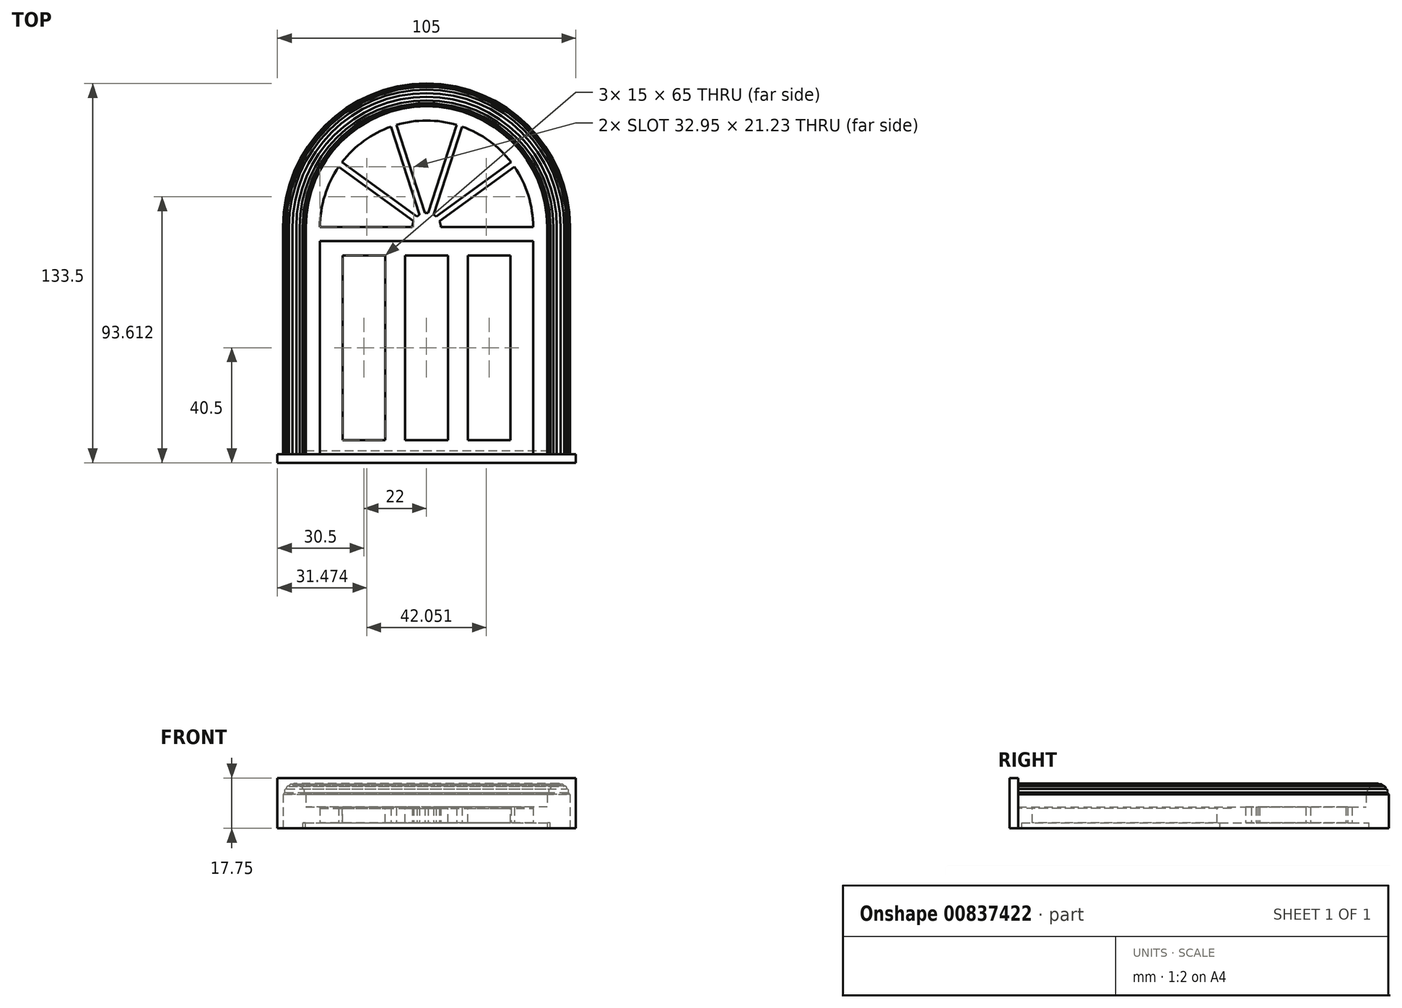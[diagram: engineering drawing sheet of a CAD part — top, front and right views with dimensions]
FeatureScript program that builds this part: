
annotation { "Feature Type Name" : "Feature", "Feature Type Description" : "" }
export const myFeature = defineFeature(function(context is Context, id is Id, definition is map)
    precondition{}
    {
        {
            var Q0;
            Q0=qCreatedBy(makeId("Top.planeOp"),FACE);
            var sketch = newSketch(context, id + "F0", { "sketchPlane" : qUnion([Q0])});
            skLineSegment(sketch, "E0.bottom", {"start": v(-37.5, 75) * mm, "end": v(37.5, 75) * mm});
            skLineSegment(sketch, "E0.top", {"start": v(-37.5, 0) * mm, "end": v(37.5, 0) * mm});
            skLineSegment(sketch, "E0.left", {"start": v(-37.5, 75) * mm, "end": v(-37.5, 0) * mm});
            skLineSegment(sketch, "E0.right", {"start": v(37.5, 75) * mm, "end": v(37.5, 0) * mm});
            skPoint(sketch, "E1", {"position": v(0, 0) * mm});
            skSolve(sketch);
        }
        {
            var Q0;
            Q0=qSketchRegion(id+"F0",true);
            extrude(context, id + "F1", {"entities" : qUnion([Q0]), "depth" : 5 * mm, "offsetDistance" : 25 * mm});
        }
        {
            var Q0;
            Q0=makeQuery(id+"F1.opExtrude","CAP_FACE",FACE,{"disambiguationData":[OSD([sQuery(id+"F0.wireOp",EDGE,"E0.bottom"),sQuery(id+"F0.wireOp",EDGE,"E0.top"),sQuery(id+"F0.wireOp",EDGE,"E0.left"),sQuery(id+"F0.wireOp",EDGE,"E0.right")])],"isStart":false});
            var sketch = newSketch(context, id + "F2", { "sketchPlane" : qUnion([Q0])});
            skLineSegment(sketch, "E2.bottom", {"start": v(-7.5, 70) * mm, "end": v(7.5, 70) * mm});
            skLineSegment(sketch, "E2.top", {"start": v(-7.5, 5) * mm, "end": v(7.5, 5) * mm});
            skLineSegment(sketch, "E2.left", {"start": v(-7.5, 70) * mm, "end": v(-7.5, 5) * mm});
            skLineSegment(sketch, "E2.right", {"start": v(7.5, 70) * mm, "end": v(7.5, 5) * mm});
            skPoint(sketch, "E3", {"position": v(0, 5) * mm});
            skLineSegment(sketch, "E4.bottom", {"start": v(14.5, 70) * mm, "end": v(29.5, 70) * mm});
            skLineSegment(sketch, "E4.top", {"start": v(14.5, 5) * mm, "end": v(29.5, 5) * mm});
            skLineSegment(sketch, "E4.left", {"start": v(14.5, 70) * mm, "end": v(14.5, 5) * mm});
            skLineSegment(sketch, "E4.right", {"start": v(29.5, 70) * mm, "end": v(29.5, 5) * mm});
            skLineSegment(sketch, "E5.bottom", {"start": v(-29.5, 70) * mm, "end": v(-14.5, 70) * mm});
            skLineSegment(sketch, "E5.top", {"start": v(-29.5, 5) * mm, "end": v(-14.5, 5) * mm});
            skLineSegment(sketch, "E5.left", {"start": v(-29.5, 70) * mm, "end": v(-29.5, 5) * mm});
            skLineSegment(sketch, "E5.right", {"start": v(-14.5, 70) * mm, "end": v(-14.5, 5) * mm});
            skSolve(sketch);
        }
        {
            var Q0;
            Q0=qSketchRegion(id+"F2",true);
            extrude(context, id + "F3", {"entities" : qUnion([Q0]), "operationType" : NewBodyOperationType.REMOVE, "oppositeDirection" : true, "depth" : 5 * mm, "offsetDistance" : 25 * mm});
        }
        {
            var Q0;
            Q0=qCreatedBy(makeId("Top.planeOp"),FACE);
            var sketch = newSketch(context, id + "F4", { "sketchPlane" : qUnion([Q0])});
            skLineSegment(sketch, "E6.bottom", {"start": v(-42.5, 0) * mm, "end": v(-37.5, 0) * mm});
            skLineSegment(sketch, "E6.left", {"start": v(-42.5, 0) * mm, "end": v(-42.5, 80) * mm});
            skLineSegment(sketch, "E6.right", {"start": v(-37.5, 0) * mm, "end": v(-37.5, 75) * mm});
            skLineSegment(sketch, "E7", {"start": v(0, 0) * mm, "end": v(0, 80) * mm, "construction": true});
            skLineSegment(sketch, "E8.bottom", {"start": v(-37.5, 80) * mm, "end": v(-5, 80) * mm});
            skLineSegment(sketch, "E8.top", {"start": v(-37.5, 75) * mm, "end": v(0, 75) * mm});
            skLineSegment(sketch, "E8.right", {"start": v(0, 80) * mm, "end": v(0, 75) * mm});
            skArc(sketch, "E9", {"start": v(0, 117.5) * mm, "mid": v(-5.37, 117.11) * mm, "end": v(-10.63, 115.96) * mm});
            skArc(sketch, "E10", {"start": v(0, 122.5) * mm, "mid": v(-30.05, 110.05) * mm, "end": v(-42.5, 80) * mm});
            skLineSegment(sketch, "E11.trimOffspring", {"start": v(0, 117.5) * mm, "end": v(0, 122.5) * mm});
            skArc(sketch, "E12", {"start": v(0, 85) * mm, "mid": v(-0.28, 85) * mm, "end": v(-0.56, 84.97) * mm});
            skLineSegment(sketch, "E13", {"start": v(-34.38, 104.98) * mm, "end": v(0, 80) * mm, "construction": true});
            skLineSegment(sketch, "E14", {"start": v(-13.13, 120.42) * mm, "end": v(0, 80) * mm, "construction": true});
            skLineSegment(sketch, "E15", {"start": v(-30.92, 101.23) * mm, "end": v(-4.55, 82.07) * mm});
            skLineSegment(sketch, "E16", {"start": v(-3.38, 83.69) * mm, "end": v(-29.74, 102.84) * mm});
            skPoint(sketch, "E17", {"position": v(-30.33, 102.03) * mm});
            skPoint(sketch, "E18", {"position": v(-3.96, 82.88) * mm});
            skLineSegment(sketch, "E19", {"start": v(-10.63, 115.96) * mm, "end": v(-0.56, 84.97) * mm});
            skLineSegment(sketch, "E20", {"start": v(-2.46, 84.35) * mm, "end": v(-12.54, 115.34) * mm});
            skPoint(sketch, "E21", {"position": v(-11.58, 115.65) * mm});
            skPoint(sketch, "E22", {"position": v(-1.51, 84.66) * mm});
            skLineSegment(sketch, "E23", {"start": v(0, 80) * mm, "end": v(0, 85) * mm});
            skArc(sketch, "E24.trimOffspring", {"start": v(-30.92, 101.23) * mm, "mid": v(-35.82, 91.11) * mm, "end": v(-37.5, 80) * mm});
            skArc(sketch, "E25.trimOffspring", {"start": v(-12.54, 115.34) * mm, "mid": v(-22.04, 110.34) * mm, "end": v(-29.74, 102.84) * mm});
            skArc(sketch, "E26.trimOffspring", {"start": v(-4.55, 82.07) * mm, "mid": v(-4.89, 81.06) * mm, "end": v(-5, 80) * mm});
            skArc(sketch, "E27.trimOffspring", {"start": v(-2.46, 84.35) * mm, "mid": v(-2.94, 84.05) * mm, "end": v(-3.38, 83.69) * mm});
            skArc(sketch, "E28.MirrorCS", {"start": v(4.55, 82.07) * mm, "mid": v(4.89, 81.06) * mm, "end": v(5, 80) * mm});
            skArc(sketch, "E29.MirrorCS", {"start": v(0, 85) * mm, "mid": v(0.28, 85) * mm, "end": v(0.56, 84.97) * mm});
            skArc(sketch, "E30.MirrorCS", {"start": v(2.46, 84.35) * mm, "mid": v(2.94, 84.05) * mm, "end": v(3.38, 83.69) * mm});
            skLineSegment(sketch, "E31.MirrorCS", {"start": v(42.5, 0) * mm, "end": v(37.5, 0) * mm});
            skLineSegment(sketch, "E32.MirrorCS", {"start": v(37.5, 80) * mm, "end": v(5, 80) * mm});
            skLineSegment(sketch, "E33.MirrorCS", {"start": v(37.5, 75) * mm, "end": v(0, 75) * mm});
            skPoint(sketch, "E34.MirrorP", {"position": v(1.51, 84.66) * mm});
            skArc(sketch, "E35.MirrorCS", {"start": v(30.92, 101.23) * mm, "mid": v(35.82, 91.11) * mm, "end": v(37.5, 80) * mm});
            skLineSegment(sketch, "E36.MirrorCS", {"start": v(2.46, 84.35) * mm, "end": v(12.54, 115.34) * mm});
            skPoint(sketch, "E37.MirrorP", {"position": v(11.58, 115.65) * mm});
            skArc(sketch, "E38.MirrorCS", {"start": v(0, 117.5) * mm, "mid": v(5.37, 117.11) * mm, "end": v(10.63, 115.96) * mm});
            skLineSegment(sketch, "E39.MirrorCS", {"start": v(3.38, 83.69) * mm, "end": v(29.74, 102.84) * mm});
            skLineSegment(sketch, "E40.MirrorCS", {"start": v(13.13, 120.42) * mm, "end": v(0, 80) * mm, "construction": true});
            skArc(sketch, "E41.MirrorCS", {"start": v(0, 122.5) * mm, "mid": v(30.05, 110.05) * mm, "end": v(42.5, 80) * mm});
            skLineSegment(sketch, "E42.MirrorCS", {"start": v(10.63, 115.96) * mm, "end": v(0.56, 84.97) * mm});
            skPoint(sketch, "E43.MirrorP", {"position": v(30.33, 102.03) * mm});
            skLineSegment(sketch, "E44.MirrorCS", {"start": v(42.5, 0) * mm, "end": v(42.5, 80) * mm});
            skLineSegment(sketch, "E45.MirrorCS", {"start": v(34.38, 104.98) * mm, "end": v(0, 80) * mm, "construction": true});
            skArc(sketch, "E46.MirrorCS", {"start": v(12.54, 115.34) * mm, "mid": v(22.04, 110.34) * mm, "end": v(29.74, 102.84) * mm});
            skLineSegment(sketch, "E47.MirrorCS", {"start": v(30.92, 101.23) * mm, "end": v(4.55, 82.07) * mm});
            skLineSegment(sketch, "E48.MirrorCS", {"start": v(37.5, 0) * mm, "end": v(37.5, 75) * mm});
            skPoint(sketch, "E49.MirrorP", {"position": v(3.96, 82.88) * mm});
            skSolve(sketch);
        }
        {
            var Q0;
            Q0=qSketchRegion(id+"F4",true);
            extrude(context, id + "F5", {"entities" : qUnion([Q0]), "operationType" : NewBodyOperationType.ADD, "depth" : 5.5 * mm, "offsetDistance" : 25 * mm});
        }
        {
            var Q0;
            Q0=qCreatedBy(makeId("Top.planeOp"),FACE);
            var sketch = newSketch(context, id + "F6", { "sketchPlane" : qUnion([Q0])});
            skLineSegment(sketch, "E50.bottom", {"start": v(-42.5, 0) * mm, "end": v(-50.5, 0) * mm});
            skLineSegment(sketch, "E50.left", {"start": v(-42.5, 0) * mm, "end": v(-42.5, 80) * mm});
            skLineSegment(sketch, "E50.right", {"start": v(-50.5, 0) * mm, "end": v(-50.5, 80) * mm});
            skArc(sketch, "E51", {"start": v(0, 122.5) * mm, "mid": v(-30.05, 110.05) * mm, "end": v(-42.5, 80) * mm});
            skArc(sketch, "E52", {"start": v(0, 130.5) * mm, "mid": v(-35.7, 115.7) * mm, "end": v(-50.5, 80) * mm});
            skLineSegment(sketch, "E53", {"start": v(0, 122.5) * mm, "end": v(0, 130.5) * mm});
            skLineSegment(sketch, "E54.MirrorCS", {"start": v(42.5, 0) * mm, "end": v(50.5, 0) * mm});
            skLineSegment(sketch, "E55.MirrorCS", {"start": v(42.5, 0) * mm, "end": v(42.5, 80) * mm});
            skLineSegment(sketch, "E56.MirrorCS", {"start": v(50.5, 0) * mm, "end": v(50.5, 80) * mm});
            skArc(sketch, "E57.MirrorCS", {"start": v(0, 122.5) * mm, "mid": v(30.05, 110.05) * mm, "end": v(42.5, 80) * mm});
            skArc(sketch, "E58.MirrorCS", {"start": v(0, 130.5) * mm, "mid": v(35.7, 115.7) * mm, "end": v(50.5, 80) * mm});
            skSolve(sketch);
        }
        {
            var Q0;
            Q0=qSketchRegion(id+"F6",true);
            extrude(context, id + "F7", {"entities" : qUnion([Q0]), "operationType" : NewBodyOperationType.ADD, "depth" : 10 * mm, "offsetDistance" : 25 * mm});
        }
        {
            var Q0;
            Q0=makeQuery(id+"F5.opExtrude","SWEPT_FACE",FACE,{"disambiguationData":[OSD([sQuery(id+"F4.wireOp",EDGE,"E32.MirrorCS")])]});
            var sketch = newSketch(context, id + "F8", { "sketchPlane" : qUnion([Q0])});
            skLineSegment(sketch, "E59", {"start": v(46.5, 10) * mm, "end": v(44, 10) * mm});
            skCircle(sketch, "E60", {"center": v(46.5, 10) * mm, "radius": 3 * mm, "construction": true});
            skArc(sketch, "E61", {"start": v(50.25, 10) * mm, "mid": v(50.14, 10.39) * mm, "end": v(49.85, 10.67) * mm});
            skArc(sketch, "E62.1.0", {"start": v(49.85, 10.67) * mm, "mid": v(49.96, 11.44) * mm, "end": v(49.34, 11.9) * mm});
            skArc(sketch, "E62.2.0", {"start": v(49.34, 11.9) * mm, "mid": v(49.15, 12.65) * mm, "end": v(48.4, 12.84) * mm});
            skArc(sketch, "E62.3.0", {"start": v(48.4, 12.84) * mm, "mid": v(47.94, 13.46) * mm, "end": v(47.17, 13.35) * mm});
            skArc(sketch, "E62.4.0", {"start": v(47.17, 13.35) * mm, "mid": v(46.5, 13.75) * mm, "end": v(45.83, 13.35) * mm});
            skArc(sketch, "E62.5.0", {"start": v(45.83, 13.35) * mm, "mid": v(45.06, 13.46) * mm, "end": v(44.6, 12.84) * mm});
            skArc(sketch, "E62.6.0", {"start": v(44.6, 12.84) * mm, "mid": v(43.85, 12.65) * mm, "end": v(43.66, 11.9) * mm});
            skArc(sketch, "E62.7.0", {"start": v(43.66, 11.9) * mm, "mid": v(43.04, 11.44) * mm, "end": v(43.15, 10.67) * mm});
            skArc(sketch, "E62.8.0", {"start": v(43.15, 10.67) * mm, "mid": v(42.86, 10.39) * mm, "end": v(42.75, 10) * mm});
            skLineSegment(sketch, "E62.anchor2", {"start": v(46.5, 10) * mm, "end": v(44.25, 10) * mm, "construction": true});
            skLineSegment(sketch, "E63", {"start": v(46.5, 10) * mm, "end": v(50.25, 10) * mm});
            skLineSegment(sketch, "E64", {"start": v(50.25, 10) * mm, "end": v(42.75, 10) * mm});
            skLineSegment(sketch, "E65.MirrorCS", {"start": v(-46.5, 10) * mm, "end": v(-44, 10) * mm});
            skArc(sketch, "E66.MirrorCS", {"start": v(-49.85, 10.67) * mm, "mid": v(-49.96, 11.44) * mm, "end": v(-49.34, 11.9) * mm});
            skArc(sketch, "E67.MirrorCS", {"start": v(-45.83, 13.35) * mm, "mid": v(-45.06, 13.46) * mm, "end": v(-44.6, 12.84) * mm});
            skArc(sketch, "E68.MirrorCS", {"start": v(-50.25, 10) * mm, "mid": v(-50.14, 10.39) * mm, "end": v(-49.85, 10.67) * mm});
            skArc(sketch, "E69.MirrorCS", {"start": v(-44.6, 12.84) * mm, "mid": v(-43.85, 12.65) * mm, "end": v(-43.66, 11.9) * mm});
            skArc(sketch, "E70.MirrorCS", {"start": v(-47.17, 13.35) * mm, "mid": v(-46.5, 13.75) * mm, "end": v(-45.83, 13.35) * mm});
            skLineSegment(sketch, "E71.MirrorCS", {"start": v(-46.5, 10) * mm, "end": v(-44.25, 10) * mm, "construction": true});
            skArc(sketch, "E72.MirrorCS", {"start": v(-43.15, 10.67) * mm, "mid": v(-42.86, 10.39) * mm, "end": v(-42.75, 10) * mm});
            skArc(sketch, "E73.MirrorCS", {"start": v(-49.34, 11.9) * mm, "mid": v(-49.15, 12.65) * mm, "end": v(-48.4, 12.84) * mm});
            skArc(sketch, "E74.MirrorCS", {"start": v(-43.66, 11.9) * mm, "mid": v(-43.04, 11.44) * mm, "end": v(-43.15, 10.67) * mm});
            skArc(sketch, "E75.MirrorCS", {"start": v(-48.4, 12.84) * mm, "mid": v(-47.94, 13.46) * mm, "end": v(-47.17, 13.35) * mm});
            skLineSegment(sketch, "E76.MirrorCS", {"start": v(-46.5, 10) * mm, "end": v(-50.25, 10) * mm});
            skLineSegment(sketch, "E77.MirrorCS", {"start": v(-50.25, 10) * mm, "end": v(-42.75, 10) * mm});
            skCircle(sketch, "E78.MirrorC", {"center": v(-46.5, 10) * mm, "radius": 3 * mm, "construction": true});
            skSolve(sketch);
        }
        {
            var Q0;
            Q0=qSketchRegion(id+"F8",true);
            var Q1;
            Q1=makeQuery(id+"F7.opExtrude","CAP_EDGE",EDGE,{"disambiguationData":[OSD([sQuery(id+"F6.wireOp",EDGE,"E51"),sQuery(id+"F6.wireOp",EDGE,"E57.MirrorCS")])],"isStart":false});
            sweep(context, id + "F9", {"operationType" : NewBodyOperationType.ADD, "profiles" : qUnion([Q0]), "path" : qUnion([Q1])});
        }
        {
            var Q0;
            Q0=makeQuery(id+"F7.opExtrude","CAP_FACE",FACE,{"disambiguationData":[OSD([sQuery(id+"F6.wireOp",EDGE,"E50.bottom"),sQuery(id+"F6.wireOp",EDGE,"E50.left"),sQuery(id+"F6.wireOp",EDGE,"E50.right"),sQuery(id+"F6.wireOp",EDGE,"E51"),sQuery(id+"F6.wireOp",EDGE,"E52"),sQuery(id+"F6.wireOp",EDGE,"E54.MirrorCS"),sQuery(id+"F6.wireOp",EDGE,"E55.MirrorCS"),sQuery(id+"F6.wireOp",EDGE,"E56.MirrorCS"),sQuery(id+"F6.wireOp",EDGE,"E57.MirrorCS"),sQuery(id+"F6.wireOp",EDGE,"E58.MirrorCS")])],"isStart":false});
            var sketch = newSketch(context, id + "F10", { "sketchPlane" : qUnion([Q0])});
            skLineSegment(sketch, "E79", {"start": v(0, 80) * mm, "end": v(0, 130.5) * mm, "construction": true});
            skLineSegment(sketch, "E80", {"start": v(0, 80) * mm, "end": v(6.15, 130.12) * mm, "construction": true});
            skLineSegment(sketch, "E81", {"start": v(0, 80) * mm, "end": v(-6.15, 130.12) * mm, "construction": true});
            skLineSegment(sketch, "E82", {"start": v(-6.15, 130.12) * mm, "end": v(-5.18, 122.18) * mm});
            skLineSegment(sketch, "E83", {"start": v(6.15, 130.12) * mm, "end": v(5.18, 122.18) * mm});
            skArc(sketch, "E84", {"start": v(6.15, 130.12) * mm, "mid": v(0, 130.5) * mm, "end": v(-6.15, 130.12) * mm});
            skArc(sketch, "E85", {"start": v(5.18, 122.18) * mm, "mid": v(0, 122.5) * mm, "end": v(-5.18, 122.18) * mm});
            skSolve(sketch);
        }
        {
            var Q0;
            Q0 = qSketchRegion(id + "F8", true);
            var Q1;
            Q1=makeQuery(id+"F7.opExtrude","CAP_EDGE",EDGE,{"disambiguationData":[OSD([sQuery(id+"F6.wireOp",EDGE,"E50.left")])],"isStart":false});
            sweep(context, id + "F11", {"operationType" : NewBodyOperationType.ADD, "profiles" : qUnion([Q0]), "path" : qUnion([Q1])});
        }
        {
            var Q0;
            {var subQ0=sQuery(id+"F6.wireOp",EDGE,"E50.left");var subQ1=sQuery(id+"F6.wireOp",EDGE,"E50.bottom");Q0=makeQuery(id+"F11.boolean.opBoolean","MERGE",FACE,{"derivedFrom":[makeQuery(id+"F7.boolean.opBoolean","MERGE",FACE,{"derivedFrom":[makeQuery(id+"F5.boolean.opBoolean","MERGE",FACE,{"derivedFrom":[makeQuery(id+"F1.opExtrude","SWEPT_FACE",FACE,{"disambiguationData":[OSD([sQuery(id+"F0.wireOp",EDGE,"E0.top")])]}),makeQuery(id+"F5.opExtrude","SWEPT_FACE",FACE,{"disambiguationData":[OSD([sQuery(id+"F4.wireOp",EDGE,"E6.bottom")])]}),makeQuery(id+"F5.opExtrude","SWEPT_FACE",FACE,{"disambiguationData":[OSD([sQuery(id+"F4.wireOp",EDGE,"E31.MirrorCS")])]})]}),makeQuery(id+"F7.opExtrude","SWEPT_FACE",FACE,{"disambiguationData":[OSD([subQ1])]}),makeQuery(id+"F7.opExtrude","SWEPT_FACE",FACE,{"disambiguationData":[OSD([sQuery(id+"F6.wireOp",EDGE,"E54.MirrorCS")])]})]}),makeQuery(id+"F11.opSweep","CAP_FACE",FACE,{"disambiguationData":[OSD([subQ1,subQ0,sQuery(id+"F8.wireOp",EDGE,"E61"),sQuery(id+"F8.wireOp",EDGE,"E62.1.0"),sQuery(id+"F8.wireOp",EDGE,"E62.2.0"),sQuery(id+"F8.wireOp",EDGE,"E62.3.0"),sQuery(id+"F8.wireOp",EDGE,"E62.4.0"),sQuery(id+"F8.wireOp",EDGE,"E62.5.0"),sQuery(id+"F8.wireOp",EDGE,"E62.6.0"),sQuery(id+"F8.wireOp",EDGE,"E62.7.0"),sQuery(id+"F8.wireOp",EDGE,"E62.8.0"),sQuery(id+"F8.wireOp",EDGE,"E64")])],"isStart":false}),makeQuery(id+"F11.opSweep","CAP_FACE",FACE,{"disambiguationData":[OSD([subQ1,subQ0,sQuery(id+"F8.wireOp",EDGE,"E66.MirrorCS"),sQuery(id+"F8.wireOp",EDGE,"E67.MirrorCS"),sQuery(id+"F8.wireOp",EDGE,"E68.MirrorCS"),sQuery(id+"F8.wireOp",EDGE,"E69.MirrorCS"),sQuery(id+"F8.wireOp",EDGE,"E70.MirrorCS"),sQuery(id+"F8.wireOp",EDGE,"E72.MirrorCS"),sQuery(id+"F8.wireOp",EDGE,"E73.MirrorCS"),sQuery(id+"F8.wireOp",EDGE,"E74.MirrorCS"),sQuery(id+"F8.wireOp",EDGE,"E75.MirrorCS"),sQuery(id+"F8.wireOp",EDGE,"E77.MirrorCS")])],"isStart":false})]});}
            var sketch = newSketch(context, id + "F12", { "sketchPlane" : qUnion([Q0])});
            skLineSegment(sketch, "E86.bottom", {"start": v(-52.5, 0) * mm, "end": v(52.5, 0) * mm});
            skLineSegment(sketch, "E86.top", {"start": v(-52.5, 15.75) * mm, "end": v(52.5, 15.75) * mm});
            skLineSegment(sketch, "E86.left", {"start": v(-52.5, 0) * mm, "end": v(-52.5, 15.75) * mm});
            skLineSegment(sketch, "E86.right", {"start": v(52.5, 0) * mm, "end": v(52.5, 15.75) * mm});
            skSolve(sketch);
        }
        {
            var Q0;
            Q0 = qSketchRegion(id + "F12", true);
            extrude(context, id + "F13", {"entities" : qUnion([Q0]), "operationType" : NewBodyOperationType.ADD, "depth" : 3 * mm, "offsetDistance" : 25 * mm});
        }
        {
            var Q0;
            Q0=makeQuery(id+"F13.boolean.opBoolean","MERGE",FACE,{"derivedFrom":[makeQuery(id+"F7.boolean.opBoolean","MERGE",FACE,{"derivedFrom":[makeQuery(id+"F5.boolean.opBoolean","MERGE",FACE,{"derivedFrom":[makeQuery(id+"F1.opExtrude","CAP_FACE",FACE,{"disambiguationData":[OSD([sQuery(id+"F0.wireOp",EDGE,"E0.bottom"),sQuery(id+"F0.wireOp",EDGE,"E0.top"),sQuery(id+"F0.wireOp",EDGE,"E0.left"),sQuery(id+"F0.wireOp",EDGE,"E0.right")])],"isStart":true}),makeQuery(id+"F5.opExtrude","CAP_FACE",FACE,{"disambiguationData":[OSD([sQuery(id+"F4.wireOp",EDGE,"E6.bottom"),sQuery(id+"F4.wireOp",EDGE,"E6.left"),sQuery(id+"F4.wireOp",EDGE,"E6.right"),sQuery(id+"F4.wireOp",EDGE,"E8.top"),sQuery(id+"F4.wireOp",EDGE,"E9"),sQuery(id+"F4.wireOp",EDGE,"E10"),sQuery(id+"F4.wireOp",EDGE,"E8.bottom"),sQuery(id+"F4.wireOp",EDGE,"E12"),sQuery(id+"F4.wireOp",EDGE,"E15"),sQuery(id+"F4.wireOp",EDGE,"E16"),sQuery(id+"F4.wireOp",EDGE,"E19"),sQuery(id+"F4.wireOp",EDGE,"E20"),sQuery(id+"F4.wireOp",EDGE,"E24.trimOffspring"),sQuery(id+"F4.wireOp",EDGE,"E25.trimOffspring"),sQuery(id+"F4.wireOp",EDGE,"E26.trimOffspring"),sQuery(id+"F4.wireOp",EDGE,"E27.trimOffspring"),sQuery(id+"F4.wireOp",EDGE,"E28.MirrorCS"),sQuery(id+"F4.wireOp",EDGE,"E29.MirrorCS"),sQuery(id+"F4.wireOp",EDGE,"E30.MirrorCS"),sQuery(id+"F4.wireOp",EDGE,"E31.MirrorCS"),sQuery(id+"F4.wireOp",EDGE,"E33.MirrorCS"),sQuery(id+"F4.wireOp",EDGE,"E35.MirrorCS"),sQuery(id+"F4.wireOp",EDGE,"E36.MirrorCS"),sQuery(id+"F4.wireOp",EDGE,"E38.MirrorCS"),sQuery(id+"F4.wireOp",EDGE,"E39.MirrorCS"),sQuery(id+"F4.wireOp",EDGE,"E32.MirrorCS"),sQuery(id+"F4.wireOp",EDGE,"E41.MirrorCS"),sQuery(id+"F4.wireOp",EDGE,"E42.MirrorCS"),sQuery(id+"F4.wireOp",EDGE,"E44.MirrorCS"),sQuery(id+"F4.wireOp",EDGE,"E46.MirrorCS"),sQuery(id+"F4.wireOp",EDGE,"E47.MirrorCS"),sQuery(id+"F4.wireOp",EDGE,"E48.MirrorCS")])],"isStart":true})]}),makeQuery(id+"F7.opExtrude","CAP_FACE",FACE,{"disambiguationData":[OSD([sQuery(id+"F6.wireOp",EDGE,"E50.bottom"),sQuery(id+"F6.wireOp",EDGE,"E50.left"),sQuery(id+"F6.wireOp",EDGE,"E50.right"),sQuery(id+"F6.wireOp",EDGE,"E51"),sQuery(id+"F6.wireOp",EDGE,"E52"),sQuery(id+"F6.wireOp",EDGE,"E54.MirrorCS"),sQuery(id+"F6.wireOp",EDGE,"E55.MirrorCS"),sQuery(id+"F6.wireOp",EDGE,"E56.MirrorCS"),sQuery(id+"F6.wireOp",EDGE,"E57.MirrorCS"),sQuery(id+"F6.wireOp",EDGE,"E58.MirrorCS")])],"isStart":true})]}),makeQuery(id+"F13.opExtrude","SWEPT_FACE",FACE,{"disambiguationData":[OSD([sQuery(id+"F12.wireOp",EDGE,"E86.bottom")])]})]});
            var sketch = newSketch(context, id + "F14", { "sketchPlane" : qUnion([Q0])});
            skLineSegment(sketch, "E87.bottom", {"start": v(-50.5, 3) * mm, "end": v(-42.56, 3) * mm});
            skLineSegment(sketch, "E87.left", {"start": v(-50.5, 3) * mm, "end": v(-50.5, -80) * mm});
            skLineSegment(sketch, "E87.right", {"start": v(50.5, 3) * mm, "end": v(50.5, -80) * mm});
            skArc(sketch, "E88", {"start": v(-50.5, -80) * mm, "mid": v(0, -130.5) * mm, "end": v(50.5, -80) * mm});
            skLineSegment(sketch, "E89.left", {"start": v(-42.56, -1.25) * mm, "end": v(-42.56, -71) * mm});
            skLineSegment(sketch, "E89.right", {"start": v(42.56, -1.25) * mm, "end": v(42.56, -71) * mm});
            skArc(sketch, "E90", {"start": v(-42.56, -71) * mm, "mid": v(0, -123.5) * mm, "end": v(42.56, -71) * mm});
            skLineSegment(sketch, "E91.trimOffspring", {"start": v(42.56, 3) * mm, "end": v(50.5, 3) * mm});
            skLineSegment(sketch, "E92.left", {"start": v(-42.56, 3) * mm, "end": v(-42.56, 3) * mm});
            skLineSegment(sketch, "E92.right", {"start": v(42.56, 3) * mm, "end": v(42.56, 3) * mm});
            skLineSegment(sketch, "E93.bottom", {"start": v(-42.56, 3) * mm, "end": v(42.56, 3) * mm});
            skLineSegment(sketch, "E93.top", {"start": v(-42.56, -1.25) * mm, "end": v(42.56, -1.25) * mm});
            skLineSegment(sketch, "E94.bottom", {"start": v(-50.5, 3) * mm, "end": v(-52.5, 3) * mm});
            skLineSegment(sketch, "E94.top", {"start": v(-50.5, 0) * mm, "end": v(-52.5, 0) * mm});
            skLineSegment(sketch, "E94.left", {"start": v(-50.5, 3) * mm, "end": v(-50.5, 0) * mm});
            skLineSegment(sketch, "E94.right", {"start": v(-52.5, 3) * mm, "end": v(-52.5, 0) * mm});
            skLineSegment(sketch, "E95.bottom", {"start": v(52.5, 3) * mm, "end": v(50.5, 3) * mm});
            skLineSegment(sketch, "E95.top", {"start": v(52.5, 0) * mm, "end": v(50.5, 0) * mm});
            skLineSegment(sketch, "E95.left", {"start": v(52.5, 3) * mm, "end": v(52.5, 0) * mm});
            skLineSegment(sketch, "E95.right", {"start": v(50.5, 3) * mm, "end": v(50.5, 0) * mm});
            skSolve(sketch);
        }
        {
            var Q0;
            {var subQ5=sQuery(id+"F14.wireOp",EDGE,"E95.bottom");var subQ7=sQuery(id+"F14.wireOp",EDGE,"E87.bottom");var subQ11=sQuery(id+"F14.wireOp",EDGE,"E94.bottom");Q0=qUnion([makeQuery(id+"F14.imprint","IMPRINT",FACE,{"disambiguationData":[TD([[makeQuery(id+"F14.imprint","IMPRINT",EDGE,{"derivedFrom":subQ11}),-1.0]])]}),makeQuery(id+"F14.imprint","IMPRINT",FACE,{"disambiguationData":[TD([[makeQuery(id+"F14.imprint","IMPRINT",EDGE,{"derivedFrom":subQ5}),-1.0]])]}),makeQuery(id+"F14.imprint","IMPRINT",FACE,{"disambiguationData":[TD([[makeQuery(id+"F14.imprint","IMPRINT",EDGE,{"derivedFrom":subQ7}),-1.0]])]})]);}
            extrude(context, id + "F15", {"entities" : qUnion([Q0]), "operationType" : NewBodyOperationType.ADD, "depth" : 2 * mm, "offsetDistance" : 25 * mm});
        }
    });
